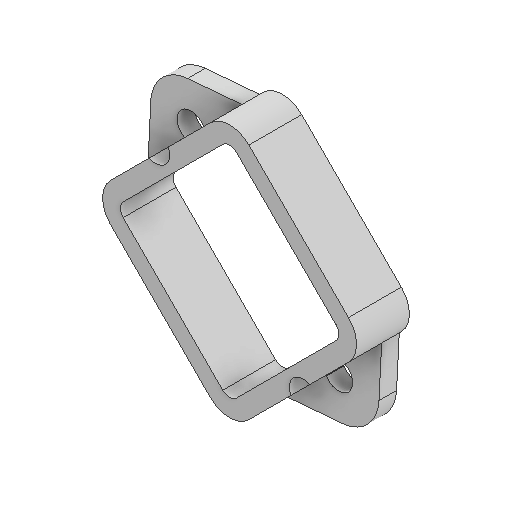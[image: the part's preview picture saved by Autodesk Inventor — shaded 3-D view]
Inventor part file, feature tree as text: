
AUTODESK INVENTOR PART (.ipt)
format: ipt  version: 2022 (Build 260153000, 153)  size: 198,144 bytes
history: native  units: mm
features: reference x4, other x3, extrude x2, sketch x2, projected_geometry x1
ambient origin geometry x8: Origin, YZ Plane, XZ Plane, XY Plane, X Axis, Y Axis, Z Axis, Center Point
bodies: Body1 (feature_tree)
feature tree (12):
  extrude  "Extrusion4"  Depth=3.2mm
  extrude  "Extrusion5"  Depth=4.0mm
  sketch  "Skizze1"  dims[d15=0.1mm d16=3.2mm]
  reference  "Referenz1"
  reference  "Referenz2"
  reference  "Referenz3"
  reference  "Referenz7"
  sketch  "Skizze5"  dims[d17=3.2mm d18=3.0mm d19=3.0mm d20=2.0mm d21=2.0mm d22=0.0mm d23=4.0mm d24=0.0mm]
  projected_geometry  "Projizierte Kontur2"
  other  "Assembly_Matchboxscope_injectionmolded.iam"
  other  "IM_Matchboxscope_base:1"
  other  "00_CCTV_M12_VCM_large:1"
